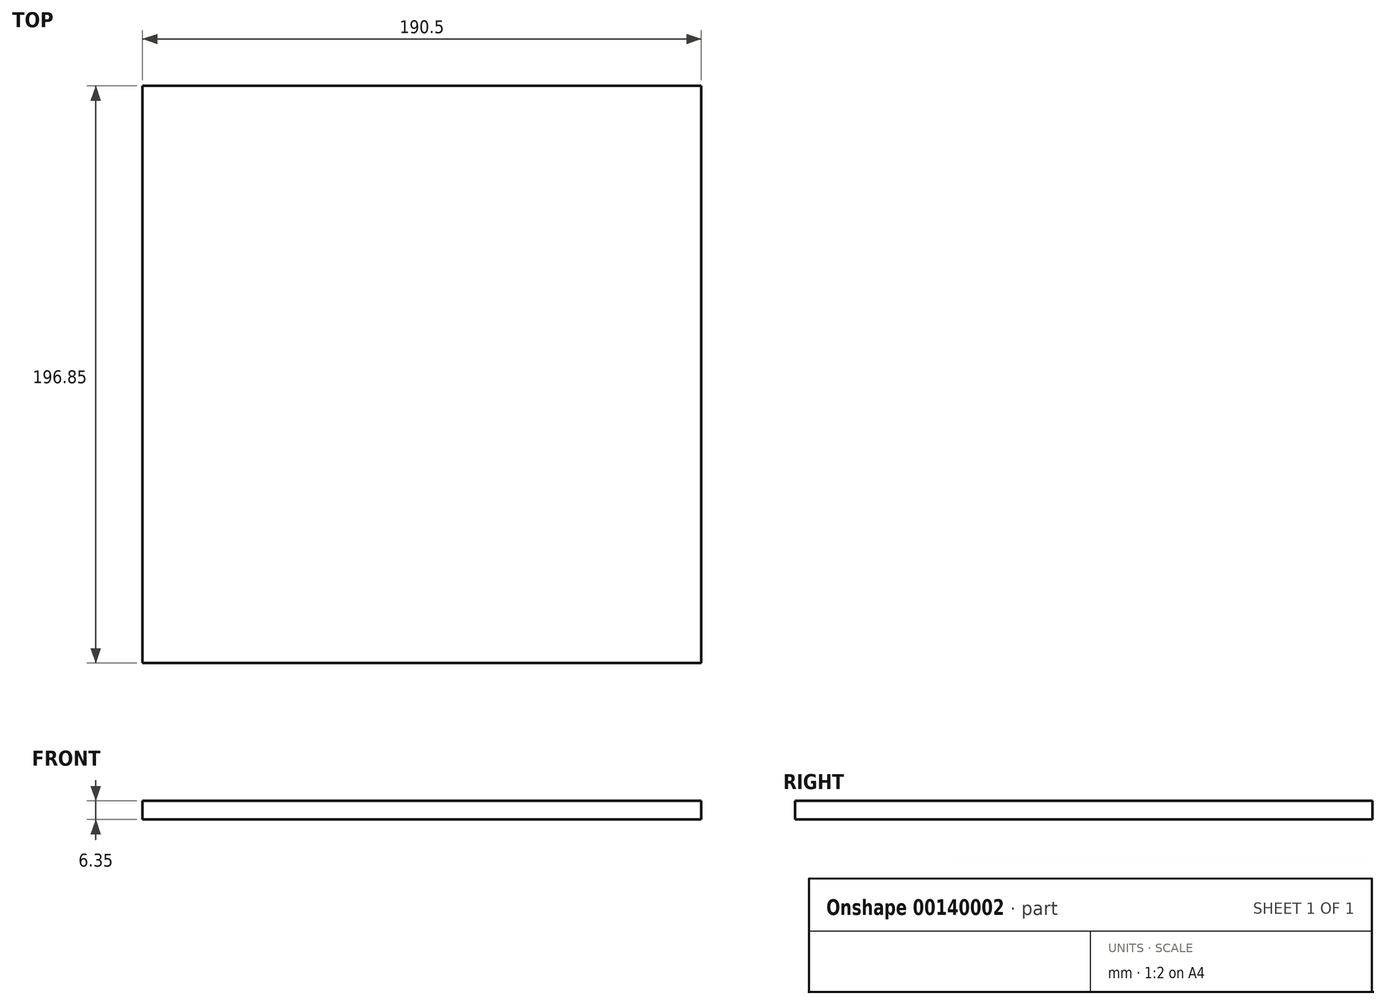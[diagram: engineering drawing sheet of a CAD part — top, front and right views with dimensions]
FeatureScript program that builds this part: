
annotation { "Feature Type Name" : "Feature", "Feature Type Description" : "" }
export const myFeature = defineFeature(function(context is Context, id is Id, definition is map)
    precondition{}
    {
        {
            var Q0;
            Q0=qCreatedBy(makeId("Top.planeOp"),FACE);
            var sketch = newSketch(context, id + "F0", { "sketchPlane" : qUnion([Q0])});
            skLineSegment(sketch, "E0.bottom", {"start": v(-105.2, 86.56) * mm, "end": v(85.3, 86.56) * mm});
            skLineSegment(sketch, "E0.top", {"start": v(-105.2, -110.29) * mm, "end": v(85.3, -110.29) * mm});
            skLineSegment(sketch, "E0.left", {"start": v(-105.2, 86.56) * mm, "end": v(-105.2, -110.29) * mm});
            skLineSegment(sketch, "E0.right", {"start": v(85.3, 86.56) * mm, "end": v(85.3, -110.29) * mm});
            skSolve(sketch);
        }
        {
            var Q0;
            Q0=makeQuery(id+"F0.imprint","IMPRINT",FACE,{"disambiguationData":[TD([[makeQuery(id+"F0.imprint","IMPRINT",EDGE,{"derivedFrom":sQuery(id+"F0.wireOp",EDGE,"E0.bottom")}),-1.0]])]});
            extrude(context, id + "F1", {"entities" : qUnion([Q0]), "depth" : 6.35 * mm});
        }
    });
